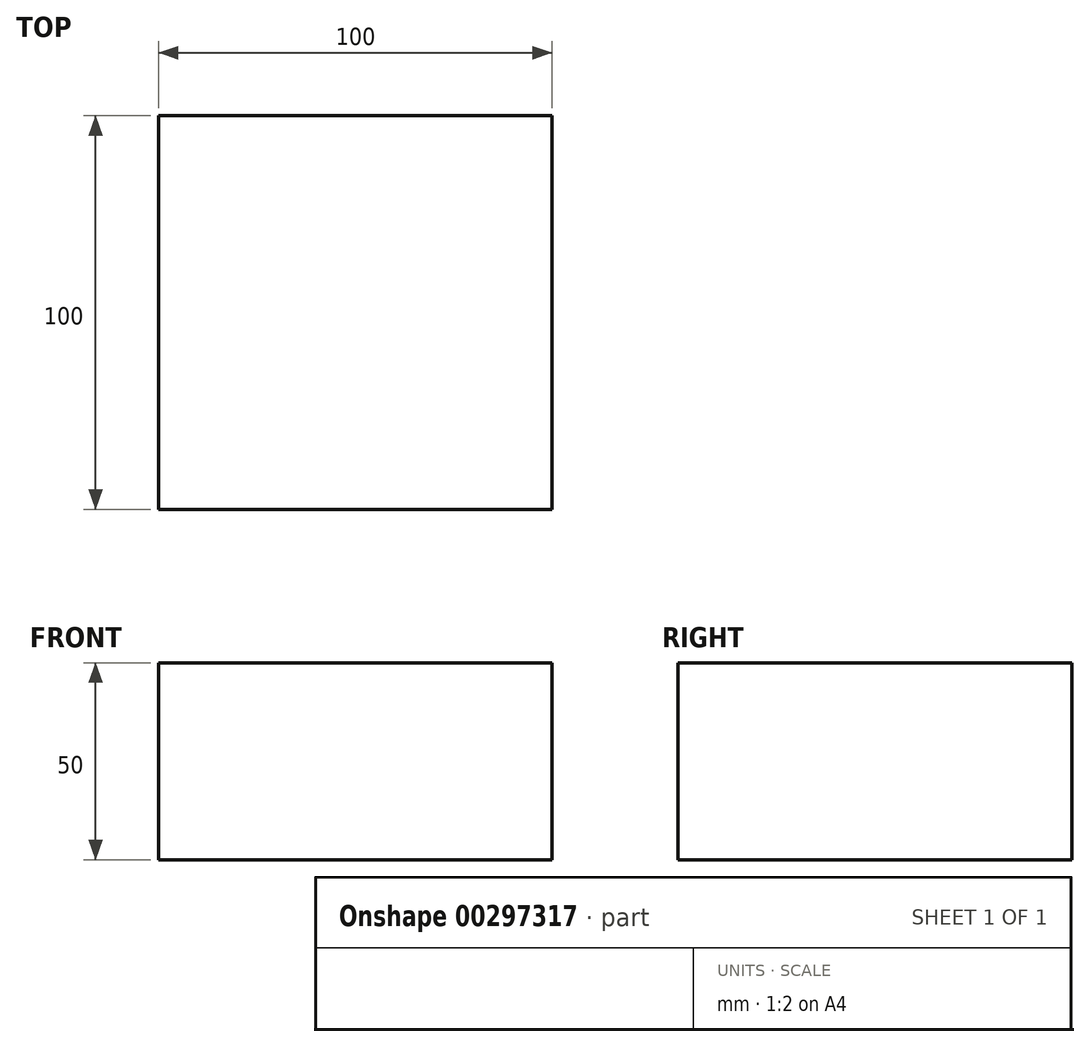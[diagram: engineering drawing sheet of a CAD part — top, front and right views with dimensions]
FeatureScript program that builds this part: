
annotation { "Feature Type Name" : "Feature", "Feature Type Description" : "" }
export const myFeature = defineFeature(function(context is Context, id is Id, definition is map)
    precondition{}
    {
        {
            var Q0;
            Q0=qCreatedBy(makeId("Top.planeOp"),FACE);
            var sketch = newSketch(context, id + "F0", { "sketchPlane" : qUnion([Q0])});
            skLineSegment(sketch, "E0.bottom", {"start": v(50, 50) * mm, "end": v(-50, 50) * mm});
            skLineSegment(sketch, "E0.top", {"start": v(50, -50) * mm, "end": v(-50, -50) * mm});
            skLineSegment(sketch, "E0.left", {"start": v(50, 50) * mm, "end": v(50, -50) * mm});
            skLineSegment(sketch, "E0.right", {"start": v(-50, 50) * mm, "end": v(-50, -50) * mm});
            skPoint(sketch, "E0.middle", {"position": v(0, 0) * mm});
            skSolve(sketch);
        }
        {
            var Q0;
            Q0=makeQuery(id+"F0.imprint","IMPRINT",FACE,{"disambiguationData":[TD([[makeQuery(id+"F0.imprint","IMPRINT",EDGE,{"derivedFrom":sQuery(id+"F0.wireOp",EDGE,"E0.bottom")}),1.0]])]});
            extrude(context, id + "F1", {"entities" : qUnion([Q0]), "endBound" : BoundingType.SYMMETRIC, "depth" : 50 * mm});
        }
    });
